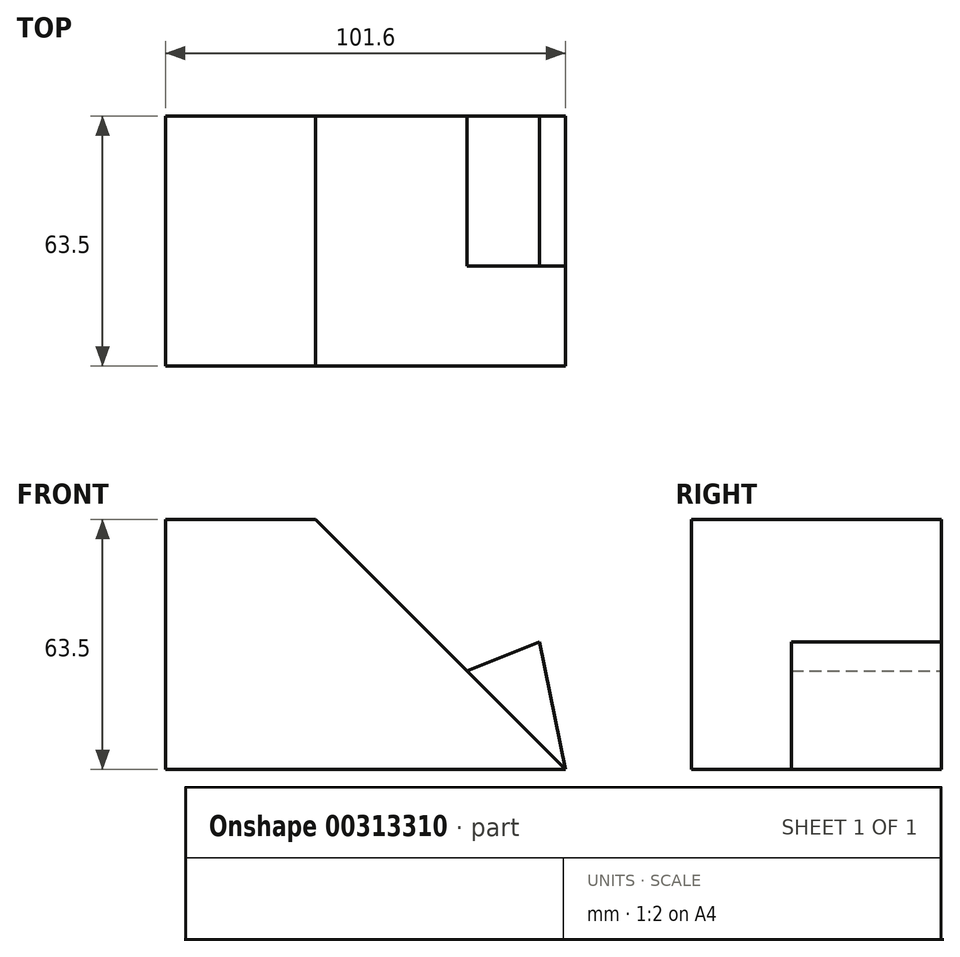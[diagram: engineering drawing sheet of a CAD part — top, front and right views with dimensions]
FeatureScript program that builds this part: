
annotation { "Feature Type Name" : "Feature", "Feature Type Description" : "" }
export const myFeature = defineFeature(function(context is Context, id is Id, definition is map)
    precondition{}
    {
        {
            var Q0;
            Q0=qCreatedBy(makeId("Front.planeOp"),FACE);
            var sketch = newSketch(context, id + "F0", { "sketchPlane" : qUnion([Q0])});
            skLineSegment(sketch, "E0", {"start": v(-50.76, -43.2) * mm, "end": v(50.84, -43.2) * mm});
            skLineSegment(sketch, "E1", {"start": v(50.84, -43.2) * mm, "end": v(-12.66, 20.3) * mm});
            skLineSegment(sketch, "E2", {"start": v(-12.66, 20.3) * mm, "end": v(-50.76, 20.3) * mm});
            skLineSegment(sketch, "E3", {"start": v(-50.76, 20.3) * mm, "end": v(-50.76, -43.2) * mm});
            skSolve(sketch);
        }
        {
            var Q0;
            Q0=makeQuery(id+"F0.imprint","IMPRINT",FACE,{"disambiguationData":[TD([[makeQuery(id+"F0.imprint","IMPRINT",EDGE,{"derivedFrom":sQuery(id+"F0.wireOp",EDGE,"E0")}),1.0]])]});
            extrude(context, id + "F1", {"entities" : qUnion([Q0]), "depth" : 63.5 * mm});
        }
        {
            var Q0;
            Q0=makeQuery(id+"F1.opExtrude","CAP_FACE",FACE,{"disambiguationData":[OSD([sQuery(id+"F0.wireOp",EDGE,"E0"),sQuery(id+"F0.wireOp",EDGE,"E1"),sQuery(id+"F0.wireOp",EDGE,"E2"),sQuery(id+"F0.wireOp",EDGE,"E3")])],"isStart":true});
            var sketch = newSketch(context, id + "F2", { "sketchPlane" : qUnion([Q0])});
            skLineSegment(sketch, "E4", {"start": v(-25.77, -18.14) * mm, "end": v(-44.2, -10.83) * mm});
            skLineSegment(sketch, "E5", {"start": v(-44.2, -10.83) * mm, "end": v(-50.84, -43.2) * mm});
            skLineSegment(sketch, "E6", {"start": v(-50.84, -43.2) * mm, "end": v(-25.77, -18.14) * mm});
            skSolve(sketch);
        }
        {
            var Q0;
            Q0=makeQuery(id+"F2.imprint","IMPRINT",FACE,{"disambiguationData":[TD([[makeQuery(id+"F2.imprint","IMPRINT",EDGE,{"derivedFrom":sQuery(id+"F2.wireOp",EDGE,"E4")}),1.0]])]});
            extrude(context, id + "F3", {"entities" : qUnion([Q0]), "oppositeDirection" : true, "depth" : 38.1 * mm});
        }
    });
